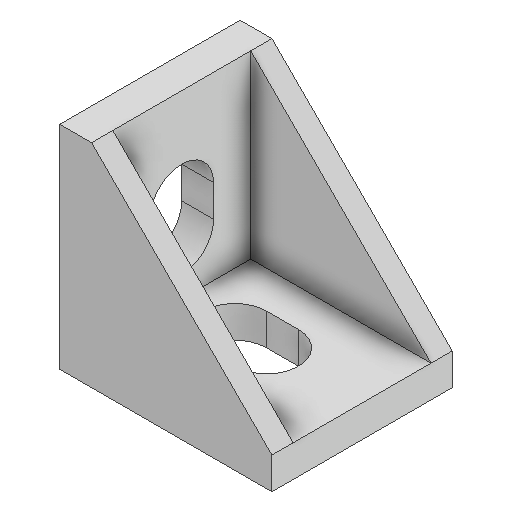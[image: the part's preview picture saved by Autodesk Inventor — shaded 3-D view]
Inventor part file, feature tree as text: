
AUTODESK INVENTOR PART (.ipt)
format: ipt  version: 2024.1 (Build 281209000, 209)  size: 153,088 bytes
history: native  units: in
note: dims shown in document units (in); Inventor stores cm internally (conversion verified against a paired STEP export)
features: extrude x3, plane x1, pattern_circular x1
ambient origin geometry x8: Origin, YZ Plane, XZ Plane, XY Plane, X Axis, Y Axis, Z Axis, Center Point
bodies: Solid1 (feature_tree)
feature tree (5):
  extrude  "Extrusion1"  Depth=0.7874in
  plane  "Work Plane1"
  extrude  "Extrusion2"  Depth=0.1181in
  extrude  "Extrusion3"  Depth=0.6693in TaperAngle=0.0deg
  pattern_circular  "Circular Pattern2"  [2 undecoded]
note: 2 required parameter values undecoded (feature->parameter linkage not recoverable at this tier; creation-order binding heuristic only, values carry confidence <= 0.55)
